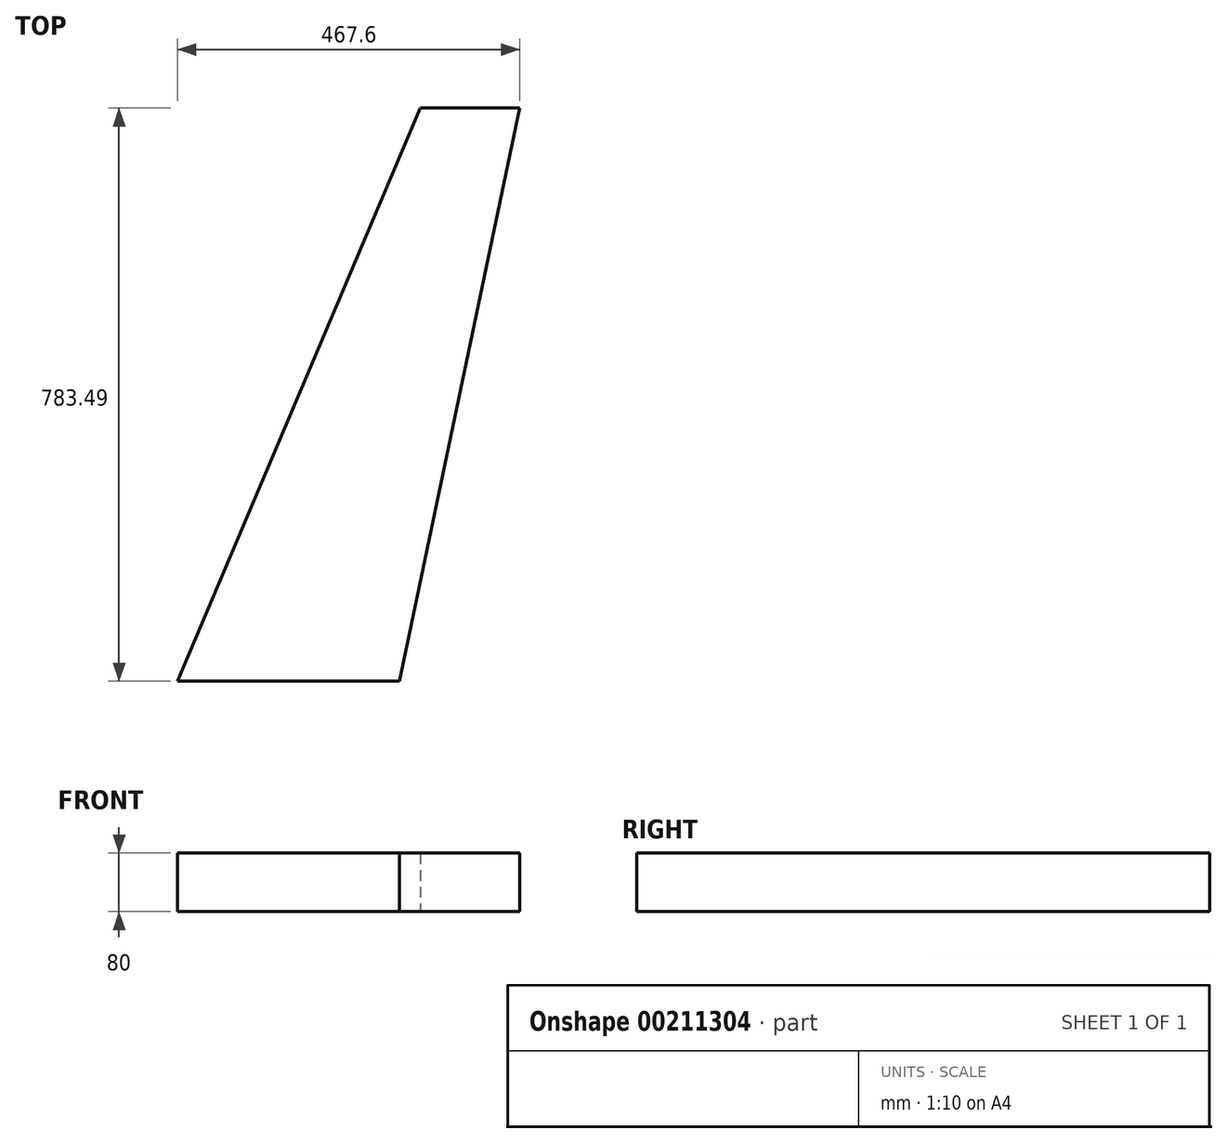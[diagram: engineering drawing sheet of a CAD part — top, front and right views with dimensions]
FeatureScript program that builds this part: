
annotation { "Feature Type Name" : "Feature", "Feature Type Description" : "" }
export const myFeature = defineFeature(function(context is Context, id is Id, definition is map)
    precondition{}
    {
        {
            var Q0;
            Q0=qCreatedBy(makeId("Top.planeOp"),FACE);
            var sketch = newSketch(context, id + "F0", { "sketchPlane" : qUnion([Q0])});
            skLineSegment(sketch, "E0", {"start": v(-772.73, -512.24) * mm, "end": v(-469.32, -512.24) * mm});
            skLineSegment(sketch, "E1", {"start": v(-772.73, -512.24) * mm, "end": v(-440.77, 271.25) * mm});
            skLineSegment(sketch, "E2", {"start": v(-469.32, -512.24) * mm, "end": v(-305.13, 271.25) * mm});
            skLineSegment(sketch, "E3", {"start": v(-440.77, 271.25) * mm, "end": v(-305.13, 271.25) * mm});
            skSolve(sketch);
        }
        {
            var Q0;
            Q0=makeQuery(id+"F0.imprint","IMPRINT",FACE,{"disambiguationData":[TD([[makeQuery(id+"F0.imprint","IMPRINT",EDGE,{"derivedFrom":sQuery(id+"F0.wireOp",EDGE,"E0")}),1.0]])]});
            extrude(context, id + "F1", {"entities" : qUnion([Q0]), "depth" : 80 * mm});
        }
    });
